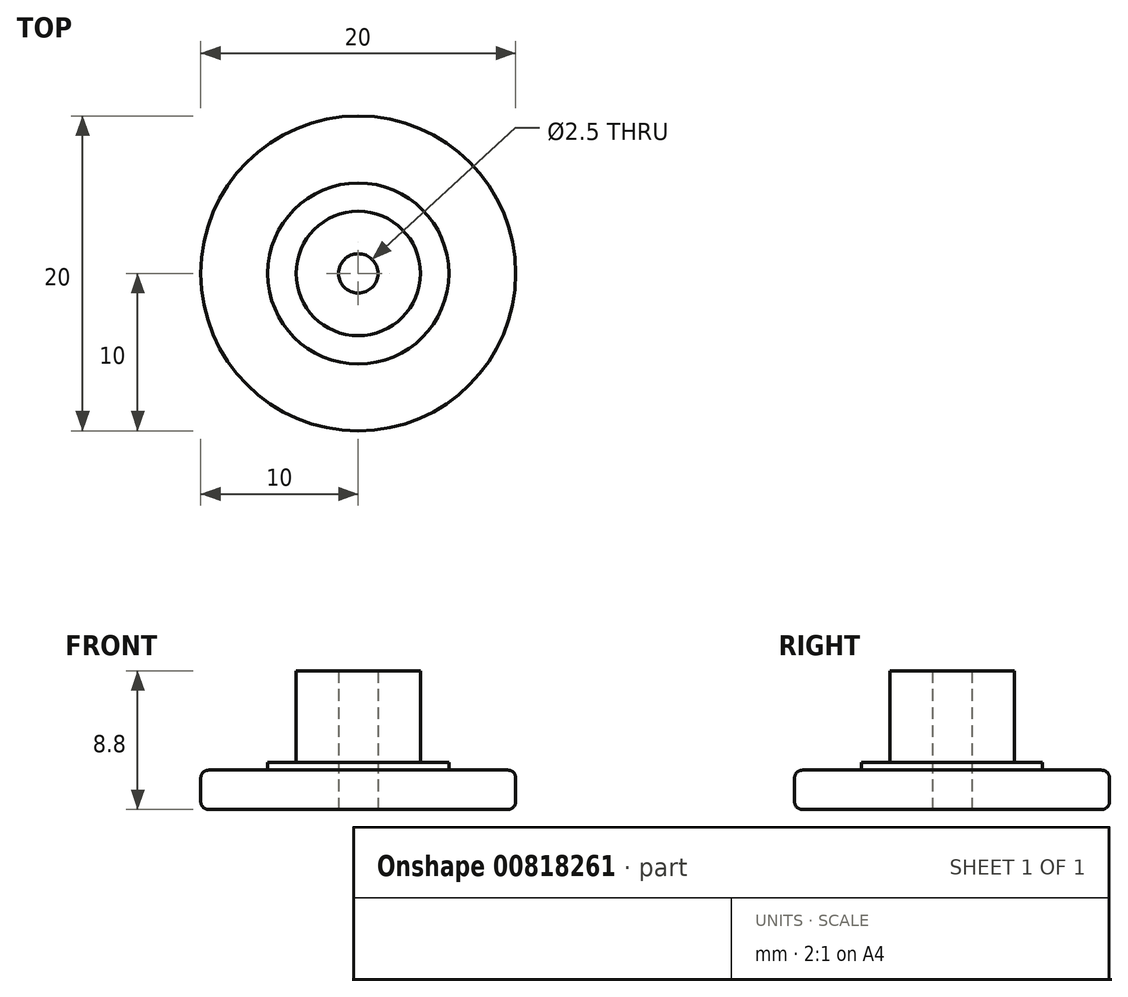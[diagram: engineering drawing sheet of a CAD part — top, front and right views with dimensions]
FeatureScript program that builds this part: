
annotation { "Feature Type Name" : "Feature", "Feature Type Description" : "" }
export const myFeature = defineFeature(function(context is Context, id is Id, definition is map)
    precondition{}
    {
        {
            var Q0;
            Q0=qCreatedBy(makeId("Top.planeOp"),FACE);
            var sketch = newSketch(context, id + "F0", { "sketchPlane" : qUnion([Q0])});
            skCircle(sketch, "E0", {"center": v(0, 0) * mm, "radius": 10 * mm});
            skCircle(sketch, "E1", {"center": v(0, 0) * mm, "radius": 1.25 * mm});
            skSolve(sketch);
        }
        {
            var Q0;
            Q0=makeQuery(id+"F0.imprint","IMPRINT",FACE,{"disambiguationData":[TD([[makeQuery(id+"F0.imprint","IMPRINT",EDGE,{"derivedFrom":sQuery(id+"F0.wireOp",EDGE,"E0")}),1.0]])]});
            extrude(context, id + "F1", {"entities" : qUnion([Q0]), "depth" : 2.5 * mm, "offsetDistance" : 25 * mm});
        }
        {
            var Q0;
            Q0=makeQuery(id+"F1.opExtrude","CAP_FACE",FACE,{"disambiguationData":[OSD([sQuery(id+"F0.wireOp",EDGE,"E0"),sQuery(id+"F0.wireOp",EDGE,"E1")])],"isStart":false});
            var sketch = newSketch(context, id + "F2", { "sketchPlane" : qUnion([Q0])});
            skCircle(sketch, "E2", {"center": v(0, 0) * mm, "radius": 5.75 * mm});
            skCircle(sketch, "E3", {"center": v(0, 0) * mm, "radius": 3.95 * mm});
            skSolve(sketch);
        }
        {
            var Q0;
            Q0=makeQuery(id+"F2.imprint","IMPRINT",FACE,{"disambiguationData":[TD([[makeQuery(id+"F2.imprint","IMPRINT",EDGE,{"derivedFrom":sQuery(id+"F2.wireOp",EDGE,"E3")}),1.0]])]});
            extrude(context, id + "F3", {"entities" : qUnion([Q0]), "operationType" : NewBodyOperationType.ADD, "depth" : 6.3 * mm, "offsetDistance" : 25 * mm});
        }
        {
            var Q0;
            Q0 = qSketchRegion(id + "F2", true);
            extrude(context, id + "F4", {"entities" : qUnion([Q0]), "operationType" : NewBodyOperationType.ADD, "depth" : 0.5 * mm, "offsetDistance" : 25 * mm});
        }
        {
            var Q0;
            Q0=makeQuery(id+"F1.opExtrude","CAP_EDGE",EDGE,{"disambiguationData":[OSD([sQuery(id+"F0.wireOp",EDGE,"E0")])],"isStart":true});
            var Q1;
            Q1=makeQuery(id+"F1.opExtrude","CAP_EDGE",EDGE,{"disambiguationData":[OSD([sQuery(id+"F0.wireOp",EDGE,"E0")])],"isStart":false});
            fillet(context, id + "F5", {"entities" : qUnion([Q0, Q1]), "radius" : 0.5 * mm, "tangentPropagation" : true, "allowEdgeOverflow" : false});
        }
    });
